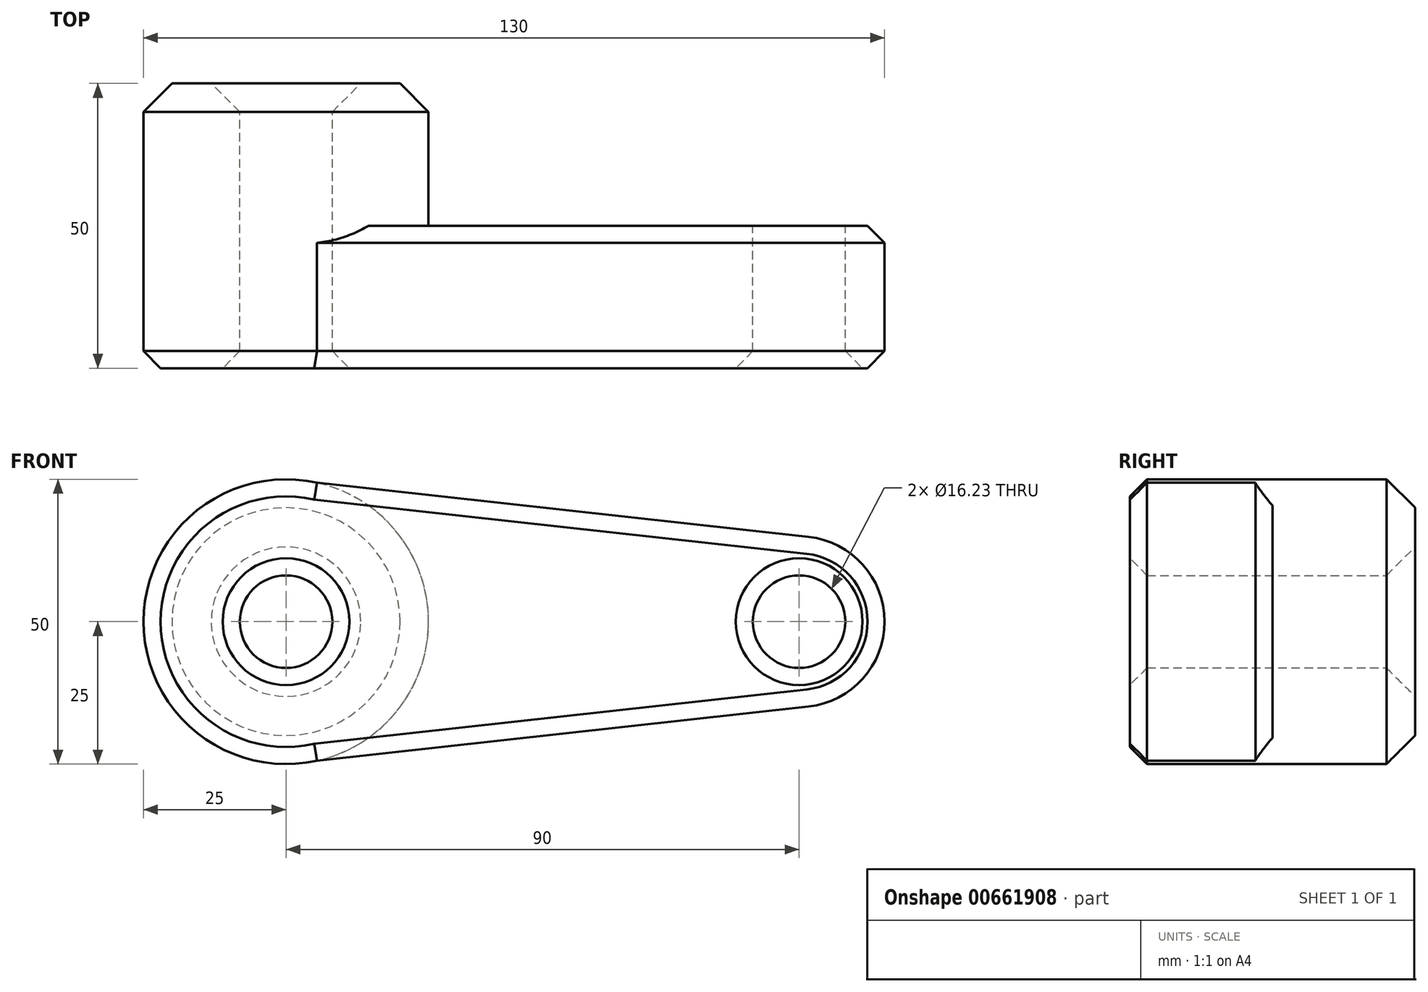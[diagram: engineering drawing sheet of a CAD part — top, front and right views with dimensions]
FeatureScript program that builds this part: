
annotation { "Feature Type Name" : "Feature", "Feature Type Description" : "" }
export const myFeature = defineFeature(function(context is Context, id is Id, definition is map)
    precondition{}
    {
        {
            var Q0;
            Q0=qCreatedBy(makeId("Front.planeOp"),FACE);
            var sketch = newSketch(context, id + "F0", { "sketchPlane" : qUnion([Q0])});
            skCircle(sketch, "E0", {"center": v(0, 0) * mm, "radius": 25 * mm});
            skCircle(sketch, "E1", {"center": v(90, 0) * mm, "radius": 15 * mm});
            skLineSegment(sketch, "E2", {"start": v(5.44, 24.4) * mm, "end": v(91.64, 14.9) * mm});
            skLineSegment(sketch, "E3", {"start": v(5.44, -24.4) * mm, "end": v(91.64, -14.9) * mm});
            skPoint(sketch, "E4.orphan", {"position": v(0, 25) * mm});
            skPoint(sketch, "E5.orphan", {"position": v(0, -25) * mm});
            skCircle(sketch, "E6", {"center": v(90, 0) * mm, "radius": 8.12 * mm});
            skCircle(sketch, "E7", {"center": v(0, 0) * mm, "radius": 8.12 * mm});
            skSolve(sketch);
        }
        {
            var Q0;
            Q0 = qSketchRegion(id + "F0", true);
            var Q1;
            Q1=sQuery(id+"F0.wireOp",EDGE,"E0");
            extrude(context, id + "F1", {"entities" : qUnion([Q0]), "surfaceEntities" : qUnion([Q1]), "depth" : 25 * mm, "offsetDistance" : 25 * mm});
        }
        {
            var Q0;
            Q0=makeQuery(id+"F1.opExtrude","CAP_FACE",FACE,{"disambiguationData":[OSD([sQuery(id+"F0.wireOp",EDGE,"E0"),sQuery(id+"F0.wireOp",EDGE,"E1"),sQuery(id+"F0.wireOp",EDGE,"E2"),sQuery(id+"F0.wireOp",EDGE,"E3"),sQuery(id+"F0.wireOp",EDGE,"E6"),sQuery(id+"F0.wireOp",EDGE,"E7")])],"isStart":false});
            chamfer(context, id + "F2", {"entities" : qUnion([Q0]), "width" : 3 * mm, "tangentPropagation" : true});
        }
        {
            var Q0;
            Q0=makeQuery(id+"F0.imprint","IMPRINT",FACE,{"disambiguationData":[TD([[makeQuery(id+"F0.imprint","IMPRINT",EDGE,{"derivedFrom":sQuery(id+"F0.wireOp",EDGE,"E7")}),-1.0]])]});
            extrude(context, id + "F3", {"entities" : qUnion([Q0]), "operationType" : NewBodyOperationType.ADD, "oppositeDirection" : true, "depth" : 25 * mm, "offsetDistance" : 25 * mm});
        }
        {
            var Q0;
            Q0=makeQuery(id+"F3.opExtrude","CAP_FACE",FACE,{"disambiguationData":[OSD([sQuery(id+"F0.wireOp",EDGE,"E0"),sQuery(id+"F0.wireOp",EDGE,"E7")])],"isStart":false});
            chamfer(context, id + "F4", {"entities" : qUnion([Q0]), "width" : 5 * mm, "tangentPropagation" : true});
        }
        {
            var Q0;
            Q0=makeQuery(id+"F1.opExtrude","CAP_EDGE",EDGE,{"disambiguationData":[OSD([sQuery(id+"F0.wireOp",EDGE,"E2")])],"isStart":true});
            chamfer(context, id + "F5", {"entities" : qUnion([Q0]), "width" : 3 * mm, "tangentPropagation" : true});
        }
    });
